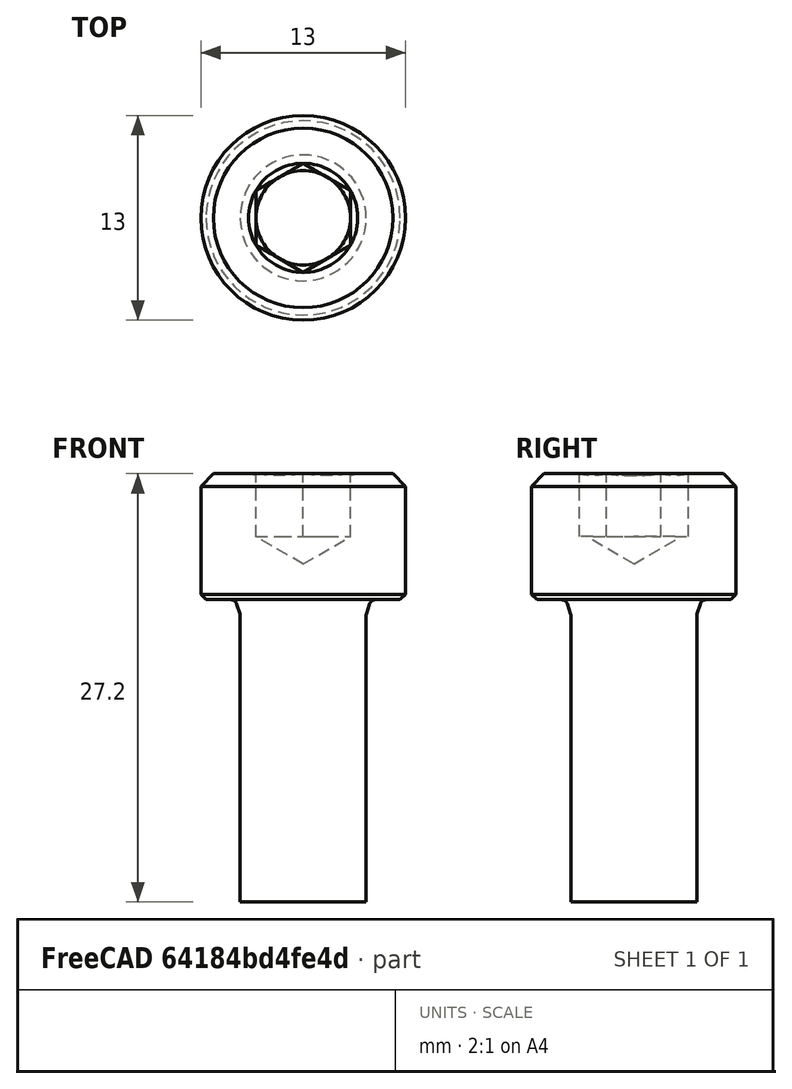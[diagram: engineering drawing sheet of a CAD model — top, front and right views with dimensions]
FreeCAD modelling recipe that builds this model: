
FCSTD DOCUMENT  (FreeCAD 0.19R24267 +99 (Git))
Label: M8x30MM cap head sawn to 19_2mm
License: All rights reserved
LicenseURL: http://en.wikipedia.org/wiki/All_rights_reserved
objects: Part::Feature×1, Sketcher::SketchObject×1, PartDesign::Pad×1, PartDesign::Body×1, Part::Cut×1
note: 6 computed .brp shape members not serialized (recipe doc carries the construction recipe); baked Part::Feature solids carry a one-line shape summary decoded from their .brp

FEATURE [Part::Feature] Part__Feature  label="TR Fastenings Ltd-M8X30mm"
  Placement = pos=(0,0,27.2) rot=(0,0,1;0rad)
  shape: bbox 13 x 13 x 38 mm, 40 faces (baked)
FEATURE [Sketcher::SketchObject] Sketch
  FullyConstrained = false
  MapMode = 5
  Support = -> [XY_Plane]
  sketch-geometry (1):
    g0: Circle CenterX=0 CenterY=0 CenterZ=0 NormalX=0 NormalY=0 NormalZ=1 AngleXU=0 Radius=12.7719
  constraints (1):
    c: Coincident(g0,g-1)
FEATURE [PartDesign::Pad] Pad
  Direction = (1,1,1)
  Length = 17
  Length2 = 100
  Profile = -> Sketch
  Reversed = true
  Type = 0
FEATURE [PartDesign::Body] Body
  Group = -> [Sketch,Pad]
  Origin = -> Origin
  Tip = -> Pad
FEATURE [Part::Cut] Cut
  Base = -> Part__Feature
  Tool = -> Body
